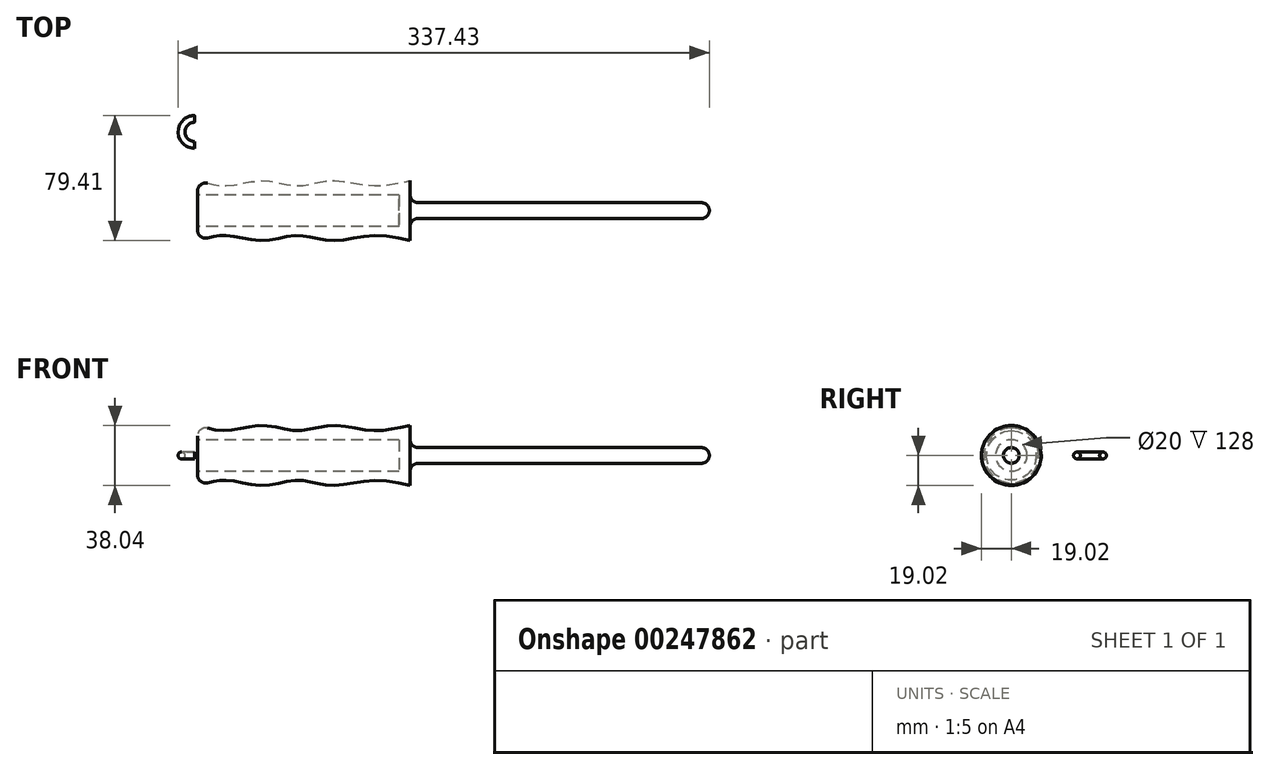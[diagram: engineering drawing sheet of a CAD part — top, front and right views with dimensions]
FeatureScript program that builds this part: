
annotation { "Feature Type Name" : "Feature", "Feature Type Description" : "" }
export const myFeature = defineFeature(function(context is Context, id is Id, definition is map)
    precondition{}
    {
        {
            var Q0;
            Q0=qCreatedBy(makeId("Top.planeOp"),FACE);
            var sketch = newSketch(context, id + "F0", { "sketchPlane" : qUnion([Q0])});
            skLineSegment(sketch, "E0", {"start": v(0, 0) * mm, "end": v(0, 19) * mm});
            skLineSegment(sketch, "E1", {"start": v(0, 0) * mm, "end": v(135, 0) * mm});
            skLineSegment(sketch, "E2", {"start": v(135, 0) * mm, "end": v(325, 0) * mm});
            skLineSegment(sketch, "E3", {"start": v(325, 0) * mm, "end": v(325, 5) * mm});
            skLineSegment(sketch, "E4", {"start": v(325, 5) * mm, "end": v(135, 5) * mm});
            skLineSegment(sketch, "E5", {"start": v(135, 5) * mm, "end": v(135, 19) * mm});
            skFitSpline(sketch, "E6", {"points": [v(0, 19) * mm, v(18.85, 15.83) * mm, v(41.4, 19) * mm, v(63.67, 15.83) * mm, v(85.03, 19) * mm, v(111.17, 15.83) * mm, v(135, 19) * mm], "startDerivative": vector(122.12, -32.58) * mm, "endDerivative": vector(154.98, 29.59) * mm});
            skSolve(sketch);
        }
        {
            var Q0;
            Q0 = qSketchRegion(id + "F0", true);
            var Q1;
            Q1=sQuery(id+"F0.wireOp",EDGE,"E1");
            revolve(context, id + "F1", {"entities" : qUnion([Q0]), "axis" : qUnion([Q1]), "revolveType" : RevolveType.FULL});
        }
        {
            var Q0;
            Q0=makeQuery(id+"F1.opRevolve","SWEPT_FACE",FACE,{"disambiguationData":[OSD([sQuery(id+"F0.wireOp",EDGE,"E4")])]});
            var Q1;
            Q1=makeQuery(id+"F1.opRevolve","SWEPT_FACE",FACE,{"disambiguationData":[OSD([sQuery(id+"F0.wireOp",EDGE,"E0")])]});
            fillet(context, id + "F2", {"entities" : qUnion([Q0, Q1]), "radius" : 5 * mm, "tangentPropagation" : true, "allowEdgeOverflow" : false});
        }
        {
            var Q0;
            Q0=makeQuery(id+"F1.opRevolve","SWEPT_FACE",FACE,{"disambiguationData":[OSD([sQuery(id+"F0.wireOp",EDGE,"E0")])]});
            var sketch = newSketch(context, id + "F3", { "sketchPlane" : qUnion([Q0])});
            skCircle(sketch, "E7", {"center": v(0, 0) * mm, "radius": 10 * mm});
            skSolve(sketch);
        }
        {
            var Q0;
            Q0 = qSketchRegion(id + "F3", true);
            extrude(context, id + "F4", {"entities" : qUnion([Q0]), "operationType" : NewBodyOperationType.REMOVE, "oppositeDirection" : true, "depth" : 128 * mm});
        }
        {
            var Q0;
            Q0=qCreatedBy(makeId("Top.planeOp"),FACE);
            var sketch = newSketch(context, id + "F5", { "sketchPlane" : qUnion([Q0])});
            skLineSegment(sketch, "E8", {"start": v(0, 49.96) * mm, "end": v(10, 49.96) * mm});
            skLineSegment(sketch, "E9", {"start": v(10, 49.96) * mm, "end": v(10, 63.9) * mm});
            skLineSegment(sketch, "E10", {"start": v(10, 63.9) * mm, "end": v(0, 63.9) * mm});
            skLineSegment(sketch, "E11", {"start": v(0, 63.9) * mm, "end": v(0, 65.9) * mm});
            skLineSegment(sketch, "E12", {"start": v(0, 65.9) * mm, "end": v(-2, 65.9) * mm});
            skLineSegment(sketch, "E13", {"start": v(-2, 65.9) * mm, "end": v(-2, 49.96) * mm});
            skLineSegment(sketch, "E14", {"start": v(-2, 49.96) * mm, "end": v(0, 49.96) * mm});
            skArc(sketch, "E15", {"start": v(-2, 41.7) * mm, "mid": v(-10.26, 49.96) * mm, "end": v(-2, 58.22) * mm});
            skSolve(sketch);
        }
        {
            var Q0;
            Q0=makeQuery(id+"F5.imprint","IMPRINT",FACE,{"disambiguationData":[TD([[makeQuery(id+"F5.imprint","IMPRINT",EDGE,{"derivedFrom":sQuery(id+"F5.wireOp",EDGE,"E8")}),1.0]])]});
            var Q1;
            Q1=sQuery(id+"F5.wireOp",EDGE,"E11");
            var Q2;
            Q2=sQuery(id+"F5.wireOp",EDGE,"E12");
            var Q3;
            Q3=sQuery(id+"F5.wireOp",EDGE,"E14");
            var Q4;
            Q4=sQuery(id+"F5.wireOp",EDGE,"E10");
            var Q5;
            Q5=sQuery(id+"F5.wireOp",EDGE,"E8");
            var Q6;
            Q6=sQuery(id+"F5.wireOp",EDGE,"E9");
            var Q7;
            Q7=sQuery(id+"F5.wireOp",EDGE,"E13");
            var Q8;
            Q8=sQuery(id+"F5.wireOp",EDGE,"E14");
            revolve(context, id + "F6", {"entities" : qUnion([Q0]), "surfaceEntities" : qUnion([Q1, Q2, Q3, Q4, Q5, Q6, Q7]), "axis" : qUnion([Q8]), "revolveType" : RevolveType.FULL});
        }
        {
            var Q0;
            Q0=makeQuery(id+"F6.opRevolve","SWEPT_FACE",FACE,{"disambiguationData":[OSD([sQuery(id+"F5.wireOp",EDGE,"E13")])]});
            var sketch = newSketch(context, id + "F7", { "sketchPlane" : qUnion([Q0])});
            skLineSegment(sketch, "E16", {"start": v(-49.96, 0) * mm, "end": v(-41.68, 0) * mm});
            skCircle(sketch, "E17", {"center": v(-41.68, 0) * mm, "radius": 2.15 * mm});
            skSolve(sketch);
        }
        {
            var Q0;
            Q0=makeQuery(id+"F7.imprint","IMPRINT",FACE,{"disambiguationData":[TD([[makeQuery(id+"F7.imprint","IMPRINT",EDGE,{"derivedFrom":sQuery(id+"F7.wireOp",EDGE,"E17")}),1.0]])]});
            var Q1;
            Q1=sQuery(id+"F5.wireOp",EDGE,"E15");
            sweep(context, id + "F8", {"profiles" : qUnion([Q0]), "path" : qUnion([Q1])});
        }
        {
            var Q0;
            Q0=makeQuery(id+"F6.opRevolve","SWEPT_FACE",FACE,{"disambiguationData":[OSD([sQuery(id+"F5.wireOp",EDGE,"E9")])]});
            var sketch = newSketch(context, id + "F9", { "sketchPlane" : qUnion([Q0])});
            skCircle(sketch, "E18", {"center": v(49.96, 0) * mm, "radius": 10.95 * mm});
            skSolve(sketch);
        }
        {
            var Q0;
            Q0 = qSketchRegion(id + "F9", true);
            extrude(context, id + "F10", {"entities" : qUnion([Q0]), "operationType" : NewBodyOperationType.REMOVE, "oppositeDirection" : true, "depth" : 9 * mm});
        }
        {
            var Q0;
            Q0=makeQuery(id+"F6.opRevolve","SWEPT_FACE",FACE,{"disambiguationData":[OSD([sQuery(id+"F5.wireOp",EDGE,"E9")])]});
            chamfer(context, id + "F11", {"entities" : qUnion([Q0]), "width" : 1 * mm, "tangentPropagation" : true});
        }
        {
            var Q0;
            Q0=makeQuery(id+"F6.opRevolve","SWEPT_BODY",BODY,{"disambiguationData":[OSD([sQuery(id+"F5.wireOp",EDGE,"E8"),sQuery(id+"F5.wireOp",EDGE,"E9"),sQuery(id+"F5.wireOp",EDGE,"E10"),sQuery(id+"F5.wireOp",EDGE,"E11"),sQuery(id+"F5.wireOp",EDGE,"E12"),sQuery(id+"F5.wireOp",EDGE,"E13"),sQuery(id+"F5.wireOp",EDGE,"E14")])]});
            deleteBodies(context, id + "F12", {"entities" : qUnion([Q0])});
        }
        {
            var Q0;
            Q0 = qSketchRegion(id + "F0", true);
            var Q1;
            Q1=sQuery(id+"F0.wireOp",EDGE,"E1");
            revolve(context, id + "F15", {"entities" : qUnion([Q0]), "axis" : qUnion([Q1]), "revolveType" : RevolveType.FULL});
        }
        {
            var Q0;
            Q0=makeQuery(id+"F15.opRevolve","SWEPT_EDGE",EDGE,{"disambiguationData":[OSD([sQuery(id+"F0.wireOp",EDGE,"E4"),sQuery(id+"F0.wireOp",EDGE,"E5")])]});
            var Q1;
            Q1=makeQuery(id+"F15.opRevolve","SWEPT_EDGE",EDGE,{"disambiguationData":[OSD([sQuery(id+"F0.wireOp",EDGE,"E3"),sQuery(id+"F0.wireOp",EDGE,"E4")])]});
            var Q2;
            Q2=makeQuery(id+"F15.opRevolve","SWEPT_FACE",FACE,{"disambiguationData":[OSD([sQuery(id+"F0.wireOp",EDGE,"E0")])]});
            fillet(context, id + "F16", {"entities" : qUnion([Q0, Q1, Q2]), "radius" : 5 * mm, "tangentPropagation" : true, "allowEdgeOverflow" : false});
        }
    });
